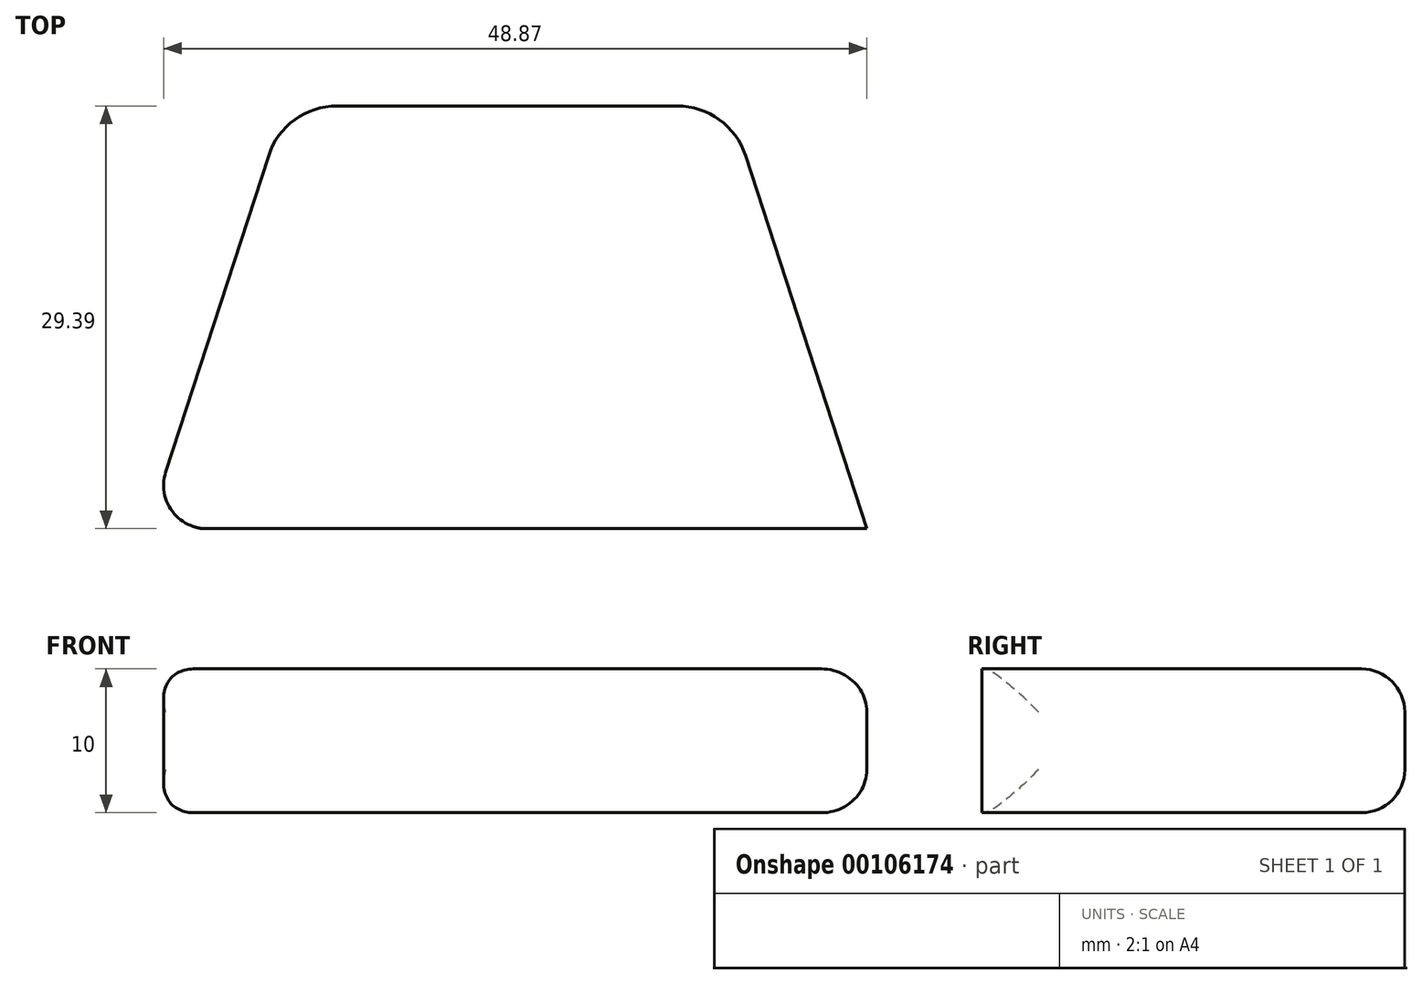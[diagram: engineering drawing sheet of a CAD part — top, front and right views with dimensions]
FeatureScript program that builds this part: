
annotation { "Feature Type Name" : "Feature", "Feature Type Description" : "" }
export const myFeature = defineFeature(function(context is Context, id is Id, definition is map)
    precondition{}
    {
        {
            var Q0;
            Q0=qCreatedBy(makeId("Top.planeOp"),FACE);
            var sketch = newSketch(context, id + "F0", { "sketchPlane" : qUnion([Q0])});
            skArc(sketch, "E0.cCircle", {"start": v(19.65, -8.12) * mm, "mid": v(0, 21.27) * mm, "end": v(-19.65, -8.12) * mm, "construction": true});
            skLineSegment(sketch, "E0.0", {"start": v(-25, -8.12) * mm, "end": v(-15.45, 21.27) * mm});
            skLineSegment(sketch, "E0.1", {"start": v(-15.45, 21.27) * mm, "end": v(15.45, 21.27) * mm});
            skLineSegment(sketch, "E0.2", {"start": v(15.45, 21.27) * mm, "end": v(25, -8.12) * mm});
            skPoint(sketch, "E0.0.midPoint", {"position": v(-20.23, 6.57) * mm});
            skLineSegment(sketch, "E1", {"start": v(-25, -8.12) * mm, "end": v(25, -8.12) * mm});
            skSolve(sketch);
        }
        {
            var Q0;
            Q0 = qSketchRegion(id + "F0", true);
            extrude(context, id + "F1", {"entities" : qUnion([Q0]), "depth" : 10 * mm});
        }
        {
            var Q0;
            Q0=makeQuery(id+"F1.opExtrude","SWEPT_EDGE",EDGE,{"disambiguationData":[OSD([sQuery(id+"F0.wireOp",EDGE,"E0.0"),sQuery(id+"F0.wireOp",EDGE,"E0.1")])]});
            var Q1;
            Q1=makeQuery(id+"F1.opExtrude","SWEPT_EDGE",EDGE,{"disambiguationData":[OSD([sQuery(id+"F0.wireOp",EDGE,"E0.1"),sQuery(id+"F0.wireOp",EDGE,"E0.2")])]});
            fillet(context, id + "F2", {"entities" : qUnion([Q0, Q1]), "radius" : 5 * mm, "tangentPropagation" : true, "allowEdgeOverflow" : false});
        }
        {
            var Q0;
            Q0=makeQuery(id+"F1.opExtrude","SWEPT_FACE",FACE,{"disambiguationData":[OSD([sQuery(id+"F0.wireOp",EDGE,"E0.0")])]});
            fillet(context, id + "F3", {"entities" : qUnion([Q0]), "radius" : 3 * mm, "tangentPropagation" : true, "allowEdgeOverflow" : false});
        }
    });
